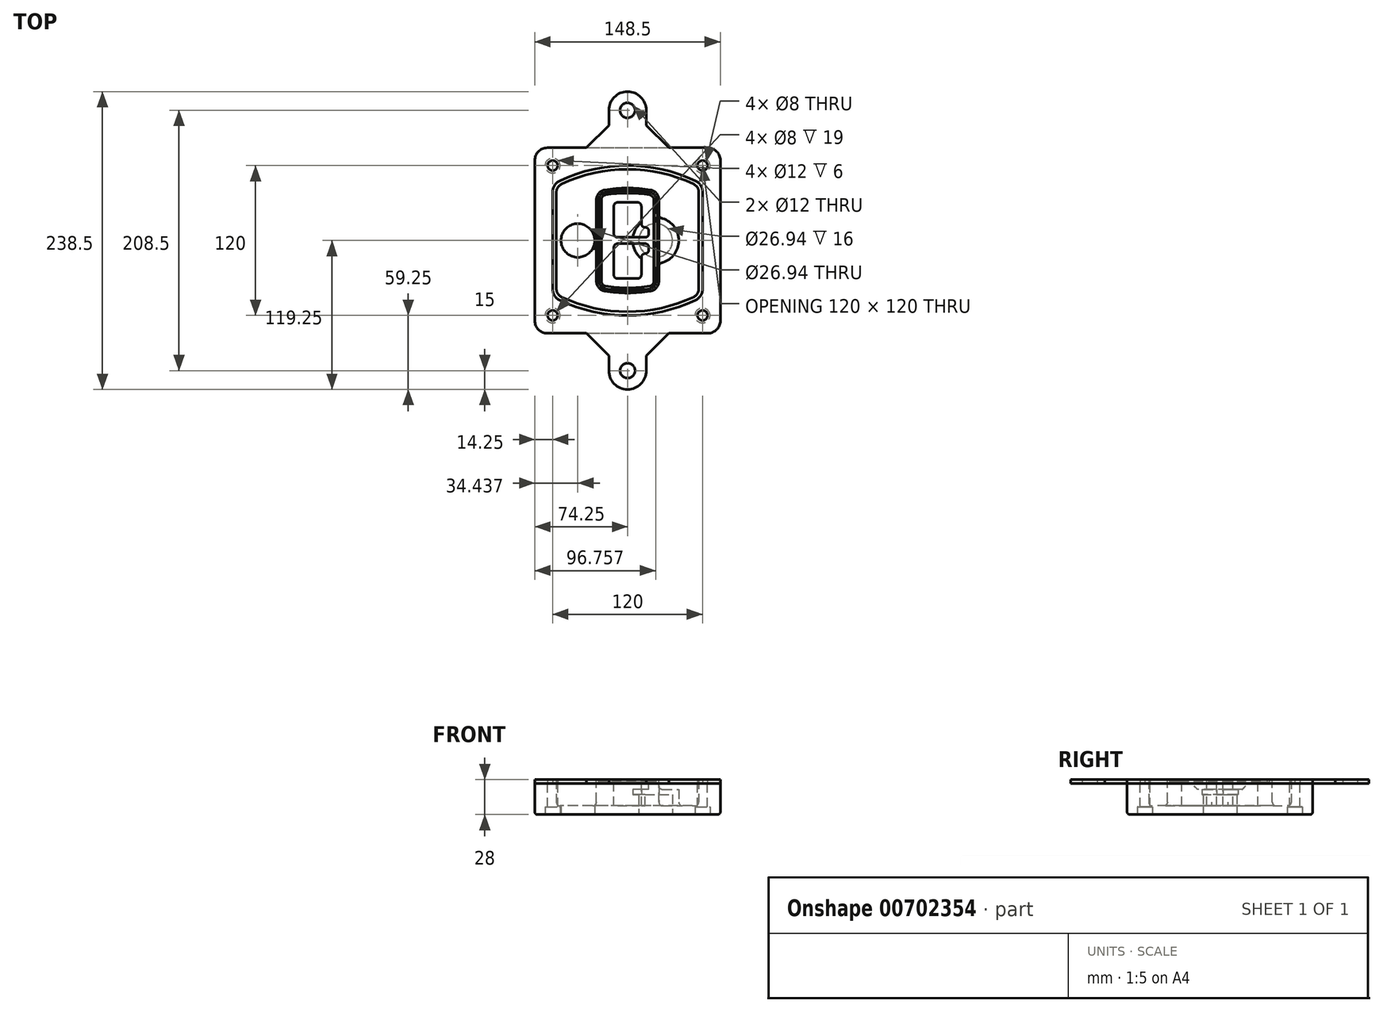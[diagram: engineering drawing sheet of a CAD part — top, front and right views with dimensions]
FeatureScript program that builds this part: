
annotation { "Feature Type Name" : "Feature", "Feature Type Description" : "" }
export const myFeature = defineFeature(function(context is Context, id is Id, definition is map)
    precondition{}
    {
        {
            var Q0;
            Q0=qCreatedBy(makeId("Top.planeOp"),FACE);
            var sketch = newSketch(context, id + "F0", { "sketchPlane" : qUnion([Q0])});
            skPoint(sketch, "E0.rect.middle", {"position": v(0, 0) * mm});
            skLineSegment(sketch, "E1.bottom", {"start": v(-64.25, -74.25) * mm, "end": v(64.25, -74.25) * mm});
            skLineSegment(sketch, "E1.top", {"start": v(-64.25, 74.25) * mm, "end": v(64.25, 74.25) * mm});
            skLineSegment(sketch, "E1.left", {"start": v(-74.25, -64.25) * mm, "end": v(-74.25, 64.25) * mm});
            skLineSegment(sketch, "E1.right", {"start": v(74.25, -64.25) * mm, "end": v(74.25, 64.25) * mm});
            skLineSegment(sketch, "E2", {"start": v(-74.25, 74.25) * mm, "end": v(74.25, -74.25) * mm, "construction": true});
            skLineSegment(sketch, "E3", {"start": v(74.25, 74.25) * mm, "end": v(-74.25, -74.25) * mm, "construction": true});
            skCircle(sketch, "E4", {"center": v(-60, 60) * mm, "radius": 4 * mm});
            skCircle(sketch, "E5", {"center": v(60, 60) * mm, "radius": 4 * mm});
            skCircle(sketch, "E6", {"center": v(60, -60) * mm, "radius": 4 * mm});
            skCircle(sketch, "E7", {"center": v(-60, -60) * mm, "radius": 4 * mm});
            skLineSegment(sketch, "E8", {"start": v(-60, 60) * mm, "end": v(60, 60) * mm, "construction": true});
            skLineSegment(sketch, "E9", {"start": v(60, 60) * mm, "end": v(60, -60) * mm, "construction": true});
            skLineSegment(sketch, "E10", {"start": v(60, -60) * mm, "end": v(-60, -60) * mm, "construction": true});
            skLineSegment(sketch, "E11", {"start": v(-60, -60) * mm, "end": v(-60, 60) * mm, "construction": true});
            skLineSegment(sketch, "E12", {"start": v(-60, 38.83) * mm, "end": v(-60, -38.83) * mm});
            skLineSegment(sketch, "E13", {"start": v(60, 38.83) * mm, "end": v(60, -38.83) * mm});
            skArc(sketch, "E14", {"start": v(54.26, 47.88) * mm, "mid": v(0, 60) * mm, "end": v(-54.26, 47.88) * mm});
            skArc(sketch, "E15", {"start": v(-54.26, -47.88) * mm, "mid": v(0, -60) * mm, "end": v(54.26, -47.88) * mm});
            skLineSegment(sketch, "E16", {"start": v(-60, 0) * mm, "end": v(60, 0) * mm, "construction": true});
            skPoint(sketch, "E17.visualSharp", {"position": v(-60, -45) * mm});
            skArc(sketch, "E17.filletArc", {"start": v(-60, -38.83) * mm, "mid": v(-58.44, -44.2) * mm, "end": v(-54.26, -47.88) * mm});
            skPoint(sketch, "E18.visualSharp", {"position": v(-60, 45) * mm});
            skArc(sketch, "E18.filletArc", {"start": v(-54.26, 47.88) * mm, "mid": v(-58.44, 44.2) * mm, "end": v(-60, 38.83) * mm});
            skPoint(sketch, "E19.visualSharp", {"position": v(60, 45) * mm});
            skArc(sketch, "E19.filletArc", {"start": v(60, 38.83) * mm, "mid": v(58.44, 44.2) * mm, "end": v(54.26, 47.88) * mm});
            skPoint(sketch, "E20.visualSharp", {"position": v(60, -45) * mm});
            skArc(sketch, "E20.filletArc", {"start": v(54.26, -47.88) * mm, "mid": v(58.44, -44.2) * mm, "end": v(60, -38.83) * mm});
            skPoint(sketch, "E21.visualSharp", {"position": v(-74.25, 74.25) * mm});
            skArc(sketch, "E21.filletArc", {"start": v(-64.25, 74.25) * mm, "mid": v(-71.32, 71.32) * mm, "end": v(-74.25, 64.25) * mm});
            skPoint(sketch, "E22.visualSharp", {"position": v(74.25, 74.25) * mm});
            skArc(sketch, "E22.filletArc", {"start": v(74.25, 64.25) * mm, "mid": v(71.32, 71.32) * mm, "end": v(64.25, 74.25) * mm});
            skPoint(sketch, "E23.visualSharp", {"position": v(74.25, -74.25) * mm});
            skArc(sketch, "E23.filletArc", {"start": v(64.25, -74.25) * mm, "mid": v(71.32, -71.32) * mm, "end": v(74.25, -64.25) * mm});
            skPoint(sketch, "E24.visualSharp", {"position": v(-74.25, -74.25) * mm});
            skArc(sketch, "E24.filletArc", {"start": v(-74.25, -64.25) * mm, "mid": v(-71.32, -71.32) * mm, "end": v(-64.25, -74.25) * mm});
            skArc(sketch, "E25.0", {"start": v(57, 38.83) * mm, "mid": v(55.9, 42.58) * mm, "end": v(52.98, 45.17) * mm});
            skLineSegment(sketch, "E25.1", {"start": v(57, 38.83) * mm, "end": v(57, -38.83) * mm});
            skArc(sketch, "E25.2", {"start": v(52.98, -45.17) * mm, "mid": v(55.9, -42.58) * mm, "end": v(57, -38.83) * mm});
            skArc(sketch, "E25.3", {"start": v(-52.98, -45.17) * mm, "mid": v(0, -57) * mm, "end": v(52.98, -45.17) * mm});
            skArc(sketch, "E25.4", {"start": v(-57, -38.83) * mm, "mid": v(-55.9, -42.58) * mm, "end": v(-52.98, -45.17) * mm});
            skArc(sketch, "E25.5", {"start": v(52.98, 45.17) * mm, "mid": v(0, 57) * mm, "end": v(-52.98, 45.17) * mm});
            skLineSegment(sketch, "E25.6", {"start": v(-57, 38.83) * mm, "end": v(-57, -38.83) * mm});
            skArc(sketch, "E25.7", {"start": v(-52.98, 45.17) * mm, "mid": v(-55.9, 42.58) * mm, "end": v(-57, 38.83) * mm});
            skArc(sketch, "E26.0", {"start": v(-55.96, 51.5) * mm, "mid": v(-61.82, 46.33) * mm, "end": v(-64, 38.83) * mm});
            skArc(sketch, "E26.1", {"start": v(55.96, 51.5) * mm, "mid": v(0, 64) * mm, "end": v(-55.96, 51.5) * mm});
            skArc(sketch, "E26.2", {"start": v(64, 38.83) * mm, "mid": v(61.82, 46.33) * mm, "end": v(55.96, 51.5) * mm});
            skLineSegment(sketch, "E26.3", {"start": v(64, 38.83) * mm, "end": v(64, -38.83) * mm});
            skArc(sketch, "E26.4", {"start": v(55.96, -51.5) * mm, "mid": v(61.82, -46.33) * mm, "end": v(64, -38.83) * mm});
            skLineSegment(sketch, "E26.5", {"start": v(-64, 38.83) * mm, "end": v(-64, -38.83) * mm});
            skArc(sketch, "E26.6", {"start": v(-55.96, -51.5) * mm, "mid": v(0, -64) * mm, "end": v(55.96, -51.5) * mm});
            skArc(sketch, "E26.7", {"start": v(-64, -38.83) * mm, "mid": v(-61.82, -46.33) * mm, "end": v(-55.96, -51.5) * mm});
            skSolve(sketch);
        }
        {
            var Q0;
            Q0=makeQuery(id+"F0.imprint","IMPRINT",FACE,{"disambiguationData":[TD([[makeQuery(id+"F0.imprint","IMPRINT",EDGE,{"derivedFrom":sQuery(id+"F0.wireOp",EDGE,"E1.bottom")}),1.0]])]});
            var Q1;
            Q1=makeQuery(id+"F0.imprint","IMPRINT",FACE,{"disambiguationData":[TD([[makeQuery(id+"F0.imprint","IMPRINT",EDGE,{"derivedFrom":sQuery(id+"F0.wireOp",EDGE,"E12")}),1.0]])]});
            var Q2;
            Q2=makeQuery(id+"F0.imprint","IMPRINT",FACE,{"disambiguationData":[TD([[makeQuery(id+"F0.imprint","IMPRINT",EDGE,{"derivedFrom":sQuery(id+"F0.wireOp",EDGE,"E25.0")}),1.0]])]});
            var Q3;
            Q3=makeQuery(id+"F0.imprint","IMPRINT",FACE,{"disambiguationData":[TD([[makeQuery(id+"F0.imprint","IMPRINT",EDGE,{"derivedFrom":sQuery(id+"F0.wireOp",EDGE,"E12")}),-1.0]])]});
            extrude(context, id + "F1", {"entities" : qUnion([Q0, Q1, Q2, Q3]), "oppositeDirection" : true, "depth" : 25 * mm});
        }
        {
            var Q0;
            Q0=makeQuery(id+"F0.imprint","IMPRINT",FACE,{"disambiguationData":[TD([[makeQuery(id+"F0.imprint","IMPRINT",EDGE,{"derivedFrom":sQuery(id+"F0.wireOp",EDGE,"E12")}),1.0]])]});
            extrude(context, id + "F2", {"entities" : qUnion([Q0]), "operationType" : NewBodyOperationType.ADD, "depth" : 3 * mm});
        }
        {
            var Q0;
            Q0=makeQuery(id+"F0.imprint","IMPRINT",FACE,{"disambiguationData":[TD([[makeQuery(id+"F0.imprint","IMPRINT",EDGE,{"derivedFrom":sQuery(id+"F0.wireOp",EDGE,"E25.0")}),1.0]])]});
            extrude(context, id + "F3", {"entities" : qUnion([Q0]), "operationType" : NewBodyOperationType.REMOVE, "oppositeDirection" : true, "depth" : 18 * mm});
        }
        {
            var Q0;
            Q0=makeQuery(id+"F2.opExtrude","CAP_FACE",FACE,{"disambiguationData":[OSD([sQuery(id+"F0.wireOp",EDGE,"E12"),sQuery(id+"F0.wireOp",EDGE,"E13"),sQuery(id+"F0.wireOp",EDGE,"E14"),sQuery(id+"F0.wireOp",EDGE,"E15"),sQuery(id+"F0.wireOp",EDGE,"E17.filletArc"),sQuery(id+"F0.wireOp",EDGE,"E18.filletArc"),sQuery(id+"F0.wireOp",EDGE,"E19.filletArc"),sQuery(id+"F0.wireOp",EDGE,"E20.filletArc"),sQuery(id+"F0.wireOp",EDGE,"E25.0"),sQuery(id+"F0.wireOp",EDGE,"E25.1"),sQuery(id+"F0.wireOp",EDGE,"E25.2"),sQuery(id+"F0.wireOp",EDGE,"E25.3"),sQuery(id+"F0.wireOp",EDGE,"E25.4"),sQuery(id+"F0.wireOp",EDGE,"E25.5"),sQuery(id+"F0.wireOp",EDGE,"E25.6"),sQuery(id+"F0.wireOp",EDGE,"E25.7")])],"isStart":false});
            var sketch = newSketch(context, id + "F4", { "sketchPlane" : qUnion([Q0])});
            skArc(sketch, "E27.0", {"start": v(-18.34, -40.45) * mm, "mid": v(0, -42) * mm, "end": v(18.34, -40.45) * mm});
            skArc(sketch, "E28.0", {"start": v(18.34, 40.45) * mm, "mid": v(0, 42) * mm, "end": v(-18.34, 40.45) * mm});
            skLineSegment(sketch, "E29", {"start": v(-25, 32.57) * mm, "end": v(-25, -32.57) * mm});
            skLineSegment(sketch, "E30", {"start": v(25, 32.57) * mm, "end": v(25, -32.57) * mm});
            skLineSegment(sketch, "E31", {"start": v(-25, 39.1) * mm, "end": v(25, 39.1) * mm, "construction": true});
            skLineSegment(sketch, "E32", {"start": v(-25, -39.1) * mm, "end": v(25, -39.1) * mm, "construction": true});
            skPoint(sketch, "E33.visualSharp", {"position": v(-25, 39.1) * mm});
            skArc(sketch, "E33.filletArc", {"start": v(-18.34, 40.45) * mm, "mid": v(-23.11, 37.73) * mm, "end": v(-25, 32.57) * mm});
            skPoint(sketch, "E34.visualSharp", {"position": v(25, 39.1) * mm});
            skArc(sketch, "E34.filletArc", {"start": v(25, 32.57) * mm, "mid": v(23.11, 37.73) * mm, "end": v(18.34, 40.45) * mm});
            skPoint(sketch, "E35.visualSharp", {"position": v(25, -39.1) * mm});
            skArc(sketch, "E35.filletArc", {"start": v(18.34, -40.45) * mm, "mid": v(23.11, -37.73) * mm, "end": v(25, -32.57) * mm});
            skPoint(sketch, "E36.visualSharp", {"position": v(-25, -39.1) * mm});
            skArc(sketch, "E36.filletArc", {"start": v(-25, -32.57) * mm, "mid": v(-23.11, -37.73) * mm, "end": v(-18.34, -40.45) * mm});
            skArc(sketch, "E37.0", {"start": v(52.98, 45.17) * mm, "mid": v(0, 57) * mm, "end": v(-52.98, 45.17) * mm});
            skArc(sketch, "E37.1", {"start": v(-52.98, 45.17) * mm, "mid": v(-55.9, 42.58) * mm, "end": v(-57, 38.83) * mm});
            skLineSegment(sketch, "E37.2", {"start": v(-57, 38.83) * mm, "end": v(-57, -38.83) * mm});
            skArc(sketch, "E37.3", {"start": v(-57, -38.83) * mm, "mid": v(-55.9, -42.58) * mm, "end": v(-52.98, -45.17) * mm});
            skArc(sketch, "E37.4", {"start": v(-52.98, -45.17) * mm, "mid": v(0, -57) * mm, "end": v(52.98, -45.17) * mm});
            skArc(sketch, "E37.5", {"start": v(52.98, -45.17) * mm, "mid": v(55.9, -42.58) * mm, "end": v(57, -38.83) * mm});
            skLineSegment(sketch, "E37.6", {"start": v(57, 38.83) * mm, "end": v(57, -38.83) * mm});
            skArc(sketch, "E37.7", {"start": v(57, 38.83) * mm, "mid": v(55.9, 42.58) * mm, "end": v(52.98, 45.17) * mm});
            skLineSegment(sketch, "E38.0", {"start": v(23, 32.57) * mm, "end": v(23, -32.57) * mm});
            skArc(sketch, "E38.1", {"start": v(18, -38.48) * mm, "mid": v(21.58, -36.44) * mm, "end": v(23, -32.57) * mm});
            skArc(sketch, "E38.2", {"start": v(-18, -38.48) * mm, "mid": v(0, -40) * mm, "end": v(18, -38.48) * mm});
            skArc(sketch, "E38.3", {"start": v(-23, -32.57) * mm, "mid": v(-21.58, -36.44) * mm, "end": v(-18, -38.48) * mm});
            skLineSegment(sketch, "E38.4", {"start": v(-23, 32.57) * mm, "end": v(-23, -32.57) * mm});
            skArc(sketch, "E38.5", {"start": v(23, 32.57) * mm, "mid": v(21.58, 36.44) * mm, "end": v(18, 38.48) * mm});
            skArc(sketch, "E38.6", {"start": v(-18, 38.48) * mm, "mid": v(-21.58, 36.44) * mm, "end": v(-23, 32.57) * mm});
            skArc(sketch, "E38.7", {"start": v(18, 38.48) * mm, "mid": v(0, 40) * mm, "end": v(-18, 38.48) * mm});
            skArc(sketch, "E39.0", {"start": v(21, 32.57) * mm, "mid": v(20.06, 35.15) * mm, "end": v(17.67, 36.5) * mm});
            skLineSegment(sketch, "E39.1", {"start": v(21, 32.57) * mm, "end": v(21, -32.57) * mm});
            skArc(sketch, "E39.2", {"start": v(17.67, -36.5) * mm, "mid": v(20.06, -35.15) * mm, "end": v(21, -32.57) * mm});
            skArc(sketch, "E39.3", {"start": v(-17.67, -36.5) * mm, "mid": v(0, -38) * mm, "end": v(17.67, -36.5) * mm});
            skArc(sketch, "E39.4", {"start": v(-21, -32.57) * mm, "mid": v(-20.06, -35.15) * mm, "end": v(-17.67, -36.5) * mm});
            skArc(sketch, "E39.5", {"start": v(17.67, 36.5) * mm, "mid": v(0, 38) * mm, "end": v(-17.67, 36.5) * mm});
            skLineSegment(sketch, "E39.6", {"start": v(-21, 32.57) * mm, "end": v(-21, -32.57) * mm});
            skArc(sketch, "E39.7", {"start": v(-17.67, 36.5) * mm, "mid": v(-20.06, 35.15) * mm, "end": v(-21, 32.57) * mm});
            skLineSegment(sketch, "E40", {"start": v(-25, 0) * mm, "end": v(25, 0) * mm, "construction": true});
            skLineSegment(sketch, "E41", {"start": v(-11, 5.5) * mm, "end": v(-11, 27.5) * mm});
            skLineSegment(sketch, "E42", {"start": v(-8, 30.5) * mm, "end": v(8, 30.5) * mm});
            skLineSegment(sketch, "E43", {"start": v(11, 27.5) * mm, "end": v(11, 13.5) * mm});
            skLineSegment(sketch, "E44", {"start": v(14, 10.5) * mm, "end": v(14, 10.5) * mm});
            skLineSegment(sketch, "E45", {"start": v(17, 7.5) * mm, "end": v(17, 5.5) * mm});
            skLineSegment(sketch, "E46", {"start": v(14, 2.5) * mm, "end": v(-8, 2.5) * mm});
            skPoint(sketch, "E47.visualSharp", {"position": v(-11, 30.5) * mm});
            skArc(sketch, "E47.filletArc", {"start": v(-8, 30.5) * mm, "mid": v(-10.12, 29.62) * mm, "end": v(-11, 27.5) * mm});
            skPoint(sketch, "E48.visualSharp", {"position": v(11, 30.5) * mm});
            skArc(sketch, "E48.filletArc", {"start": v(11, 27.5) * mm, "mid": v(10.12, 29.62) * mm, "end": v(8, 30.5) * mm});
            skPoint(sketch, "E49.visualSharp", {"position": v(11, 10.5) * mm});
            skArc(sketch, "E49.filletArc", {"start": v(11, 13.5) * mm, "mid": v(11.88, 11.38) * mm, "end": v(14, 10.5) * mm});
            skPoint(sketch, "E50.visualSharp", {"position": v(17, 10.5) * mm});
            skArc(sketch, "E50.filletArc", {"start": v(17, 7.5) * mm, "mid": v(16.12, 9.62) * mm, "end": v(14, 10.5) * mm});
            skPoint(sketch, "E51.visualSharp", {"position": v(17, 2.5) * mm});
            skArc(sketch, "E51.filletArc", {"start": v(14, 2.5) * mm, "mid": v(16.12, 3.38) * mm, "end": v(17, 5.5) * mm});
            skPoint(sketch, "E52.visualSharp", {"position": v(-11, 2.5) * mm});
            skArc(sketch, "E52.filletArc", {"start": v(-11, 5.5) * mm, "mid": v(-10.12, 3.38) * mm, "end": v(-8, 2.5) * mm});
            skLineSegment(sketch, "E53.0.MirrorCS", {"start": v(14, -2.5) * mm, "end": v(-8, -2.5) * mm});
            skArc(sketch, "E54.0.MirrorCS", {"start": v(-11, -5.5) * mm, "mid": v(-10.12, -3.38) * mm, "end": v(-8, -2.5) * mm});
            skLineSegment(sketch, "E55.0.MirrorCS", {"start": v(-11, -5.5) * mm, "end": v(-11, -27.5) * mm});
            skArc(sketch, "E56.0.MirrorCS", {"start": v(-8, -30.5) * mm, "mid": v(-10.12, -29.62) * mm, "end": v(-11, -27.5) * mm});
            skLineSegment(sketch, "E57.0.MirrorCS", {"start": v(-8, -30.5) * mm, "end": v(8, -30.5) * mm});
            skArc(sketch, "E58.0.MirrorCS", {"start": v(11, -27.5) * mm, "mid": v(10.12, -29.62) * mm, "end": v(8, -30.5) * mm});
            skLineSegment(sketch, "E59.0.MirrorCS", {"start": v(11, -27.5) * mm, "end": v(11, -13.5) * mm});
            skArc(sketch, "E60.0.MirrorCS", {"start": v(11, -13.5) * mm, "mid": v(11.88, -11.38) * mm, "end": v(14, -10.5) * mm});
            skArc(sketch, "E61.0.MirrorCS", {"start": v(17, -7.5) * mm, "mid": v(16.12, -9.62) * mm, "end": v(14, -10.5) * mm});
            skLineSegment(sketch, "E62.0.MirrorCS", {"start": v(17, -7.5) * mm, "end": v(17, -5.5) * mm});
            skArc(sketch, "E63.0.MirrorCS", {"start": v(14, -2.5) * mm, "mid": v(16.12, -3.38) * mm, "end": v(17, -5.5) * mm});
            skSolve(sketch);
        }
        {
            var Q0;
            Q0=makeQuery(id+"F4.imprint","IMPRINT",FACE,{"disambiguationData":[TD([[makeQuery(id+"F4.imprint","IMPRINT",EDGE,{"derivedFrom":sQuery(id+"F4.wireOp",EDGE,"E27.0")}),1.0]])]});
            var Q1;
            Q1=makeQuery(id+"F4.imprint","IMPRINT",FACE,{"disambiguationData":[TD([[makeQuery(id+"F4.imprint","IMPRINT",EDGE,{"derivedFrom":sQuery(id+"F4.wireOp",EDGE,"E38.0")}),-1.0]])]});
            var Q2;
            Q2=makeQuery(id+"F4.imprint","IMPRINT",FACE,{"disambiguationData":[TD([[makeQuery(id+"F4.imprint","IMPRINT",EDGE,{"derivedFrom":sQuery(id+"F4.wireOp",EDGE,"E39.0")}),1.0]])]});
            extrude(context, id + "F5", {"entities" : qUnion([Q0, Q1, Q2]), "operationType" : NewBodyOperationType.ADD, "endBound" : BoundingType.UP_TO_NEXT, "oppositeDirection" : true, "depth" : 25 * mm});
        }
        {
            var Q0;
            Q0=makeQuery(id+"F4.imprint","IMPRINT",FACE,{"disambiguationData":[TD([[makeQuery(id+"F4.imprint","IMPRINT",EDGE,{"derivedFrom":sQuery(id+"F4.wireOp",EDGE,"E38.0")}),-1.0]])]});
            extrude(context, id + "F6", {"entities" : qUnion([Q0]), "operationType" : NewBodyOperationType.REMOVE, "oppositeDirection" : true, "depth" : 2 * mm});
        }
        {
            var Q0;
            Q0=makeQuery(id+"F1.opExtrude","CAP_FACE",FACE,{"disambiguationData":[OSD([sQuery(id+"F0.wireOp",EDGE,"E1.bottom"),sQuery(id+"F0.wireOp",EDGE,"E1.top"),sQuery(id+"F0.wireOp",EDGE,"E1.left"),sQuery(id+"F0.wireOp",EDGE,"E1.right"),sQuery(id+"F0.wireOp",EDGE,"E4"),sQuery(id+"F0.wireOp",EDGE,"E5"),sQuery(id+"F0.wireOp",EDGE,"E6"),sQuery(id+"F0.wireOp",EDGE,"E7"),sQuery(id+"F0.wireOp",EDGE,"E21.filletArc"),sQuery(id+"F0.wireOp",EDGE,"E22.filletArc"),sQuery(id+"F0.wireOp",EDGE,"E23.filletArc"),sQuery(id+"F0.wireOp",EDGE,"E24.filletArc")])],"isStart":false});
            var sketch = newSketch(context, id + "F7", { "sketchPlane" : qUnion([Q0])});
            skCircle(sketch, "E64", {"center": v(22.5, 0) * mm, "radius": 13.47 * mm});
            skCircle(sketch, "E65", {"center": v(-39.81, 0) * mm, "radius": 13.47 * mm});
            skLineSegment(sketch, "E66", {"start": v(74.25, 0) * mm, "end": v(-74.25, 0) * mm});
            skCircle(sketch, "E67", {"center": v(22.5, 0) * mm, "radius": 18.47 * mm});
            skCircle(sketch, "E68", {"center": v(60, -60) * mm, "radius": 6 * mm});
            skCircle(sketch, "E69", {"center": v(-60, -60) * mm, "radius": 6 * mm});
            skCircle(sketch, "E70", {"center": v(-60, 60) * mm, "radius": 6 * mm});
            skCircle(sketch, "E71", {"center": v(60, 60) * mm, "radius": 6 * mm});
            skSolve(sketch);
        }
        {
            var Q0;
            {var subQ1=sQuery(id+"F7.wireOp",EDGE,"E66");var subQ4=sQuery(id+"F7.wireOp",EDGE,"E64");var subQ6=makeQuery(id+"F7.imprint","INTERSECT",VERTEX,{"disambiguationData":[OD(0.0)],"derivedFrom":[subQ4,subQ1]});Q0=makeQuery(id+"F7.imprint","IMPRINT",FACE,{"disambiguationData":[TD([[makeQuery(id+"F7.imprint","IMPRINT",EDGE,{"disambiguationData":[TD([[subQ6,-1.0]])],"derivedFrom":subQ4}),-1.0]])]});}
            var Q1;
            {var subQ0=sQuery(id+"F7.wireOp",EDGE,"E66");var subQ1=sQuery(id+"F7.wireOp",EDGE,"E64");var subQ3=makeQuery(id+"F7.imprint","INTERSECT",VERTEX,{"disambiguationData":[OD(0.0)],"derivedFrom":[subQ1,subQ0]});Q1=makeQuery(id+"F7.imprint","IMPRINT",FACE,{"disambiguationData":[TD([[makeQuery(id+"F7.imprint","IMPRINT",EDGE,{"disambiguationData":[TD([[subQ3,-1.0]])],"derivedFrom":subQ1}),1.0]])]});}
            var Q2;
            {var subQ0=sQuery(id+"F7.wireOp",EDGE,"E66");var subQ1=sQuery(id+"F7.wireOp",EDGE,"E64");var subQ3=makeQuery(id+"F7.imprint","INTERSECT",VERTEX,{"disambiguationData":[OD(0.0)],"derivedFrom":[subQ1,subQ0]});Q2=makeQuery(id+"F7.imprint","IMPRINT",FACE,{"disambiguationData":[TD([[makeQuery(id+"F7.imprint","IMPRINT",EDGE,{"disambiguationData":[TD([[subQ3,1.0]])],"derivedFrom":subQ1}),1.0]])]});}
            var Q3;
            {var subQ1=sQuery(id+"F7.wireOp",EDGE,"E66");var subQ4=sQuery(id+"F7.wireOp",EDGE,"E64");var subQ6=makeQuery(id+"F7.imprint","INTERSECT",VERTEX,{"disambiguationData":[OD(0.0)],"derivedFrom":[subQ4,subQ1]});Q3=makeQuery(id+"F7.imprint","IMPRINT",FACE,{"disambiguationData":[TD([[makeQuery(id+"F7.imprint","IMPRINT",EDGE,{"disambiguationData":[TD([[subQ6,1.0]])],"derivedFrom":subQ4}),-1.0]])]});}
            extrude(context, id + "F8", {"entities" : qUnion([Q0, Q1, Q2, Q3]), "operationType" : NewBodyOperationType.ADD, "oppositeDirection" : true, "depth" : 20 * mm});
        }
        {
            var Q0;
            {var subQ0=sQuery(id+"F7.wireOp",EDGE,"E66");var subQ1=sQuery(id+"F7.wireOp",EDGE,"E64");var subQ3=makeQuery(id+"F7.imprint","INTERSECT",VERTEX,{"disambiguationData":[OD(0.0)],"derivedFrom":[subQ1,subQ0]});Q0=makeQuery(id+"F7.imprint","IMPRINT",FACE,{"disambiguationData":[TD([[makeQuery(id+"F7.imprint","IMPRINT",EDGE,{"disambiguationData":[TD([[subQ3,-1.0]])],"derivedFrom":subQ1}),1.0]])]});}
            var Q1;
            {var subQ0=sQuery(id+"F7.wireOp",EDGE,"E66");var subQ1=sQuery(id+"F7.wireOp",EDGE,"E64");var subQ3=makeQuery(id+"F7.imprint","INTERSECT",VERTEX,{"disambiguationData":[OD(0.0)],"derivedFrom":[subQ1,subQ0]});Q1=makeQuery(id+"F7.imprint","IMPRINT",FACE,{"disambiguationData":[TD([[makeQuery(id+"F7.imprint","IMPRINT",EDGE,{"disambiguationData":[TD([[subQ3,1.0]])],"derivedFrom":subQ1}),1.0]])]});}
            extrude(context, id + "F9", {"entities" : qUnion([Q0, Q1]), "operationType" : NewBodyOperationType.REMOVE, "oppositeDirection" : true, "depth" : 16 * mm});
        }
        {
            var Q0;
            {var subQ0=sQuery(id+"F7.wireOp",EDGE,"E66");var subQ1=sQuery(id+"F7.wireOp",EDGE,"E65");var subQ3=makeQuery(id+"F7.imprint","INTERSECT",VERTEX,{"disambiguationData":[OD(0.0)],"derivedFrom":[subQ1,subQ0]});Q0=makeQuery(id+"F7.imprint","IMPRINT",FACE,{"disambiguationData":[TD([[makeQuery(id+"F7.imprint","IMPRINT",EDGE,{"disambiguationData":[TD([[subQ3,-1.0]])],"derivedFrom":subQ1}),1.0]])]});}
            var Q1;
            {var subQ0=sQuery(id+"F7.wireOp",EDGE,"E66");var subQ1=sQuery(id+"F7.wireOp",EDGE,"E65");var subQ3=makeQuery(id+"F7.imprint","INTERSECT",VERTEX,{"disambiguationData":[OD(0.0)],"derivedFrom":[subQ1,subQ0]});Q1=makeQuery(id+"F7.imprint","IMPRINT",FACE,{"disambiguationData":[TD([[makeQuery(id+"F7.imprint","IMPRINT",EDGE,{"disambiguationData":[TD([[subQ3,1.0]])],"derivedFrom":subQ1}),1.0]])]});}
            extrude(context, id + "F10", {"entities" : qUnion([Q0, Q1]), "operationType" : NewBodyOperationType.REMOVE, "oppositeDirection" : true, "depth" : 25 * mm});
        }
        {
            var Q0;
            Q0=makeQuery(id+"F7.imprint","IMPRINT",FACE,{"disambiguationData":[TD([[makeQuery(id+"F7.imprint","IMPRINT",EDGE,{"derivedFrom":sQuery(id+"F7.wireOp",EDGE,"E68")}),1.0]])]});
            var Q1;
            Q1=makeQuery(id+"F7.imprint","IMPRINT",FACE,{"disambiguationData":[TD([[makeQuery(id+"F7.imprint","IMPRINT",EDGE,{"derivedFrom":makeQuery(id+"F1.opExtrude","CAP_EDGE",EDGE,{"disambiguationData":[OSD([sQuery(id+"F0.wireOp",EDGE,"E5")])],"isStart":false})}),-1.0]])]});
            var Q2;
            Q2=makeQuery(id+"F7.imprint","IMPRINT",FACE,{"disambiguationData":[TD([[makeQuery(id+"F7.imprint","IMPRINT",EDGE,{"derivedFrom":sQuery(id+"F7.wireOp",EDGE,"E69")}),1.0]])]});
            var Q3;
            Q3=makeQuery(id+"F7.imprint","IMPRINT",FACE,{"disambiguationData":[TD([[makeQuery(id+"F7.imprint","IMPRINT",EDGE,{"derivedFrom":makeQuery(id+"F1.opExtrude","CAP_EDGE",EDGE,{"disambiguationData":[OSD([sQuery(id+"F0.wireOp",EDGE,"E4")])],"isStart":false})}),-1.0]])]});
            var Q4;
            Q4=makeQuery(id+"F7.imprint","IMPRINT",FACE,{"disambiguationData":[TD([[makeQuery(id+"F7.imprint","IMPRINT",EDGE,{"derivedFrom":sQuery(id+"F7.wireOp",EDGE,"E70")}),1.0]])]});
            var Q5;
            Q5=makeQuery(id+"F7.imprint","IMPRINT",FACE,{"disambiguationData":[TD([[makeQuery(id+"F7.imprint","IMPRINT",EDGE,{"derivedFrom":makeQuery(id+"F1.opExtrude","CAP_EDGE",EDGE,{"disambiguationData":[OSD([sQuery(id+"F0.wireOp",EDGE,"E7")])],"isStart":false})}),-1.0]])]});
            var Q6;
            Q6=makeQuery(id+"F7.imprint","IMPRINT",FACE,{"disambiguationData":[TD([[makeQuery(id+"F7.imprint","IMPRINT",EDGE,{"derivedFrom":sQuery(id+"F7.wireOp",EDGE,"E71")}),1.0]])]});
            var Q7;
            Q7=makeQuery(id+"F7.imprint","IMPRINT",FACE,{"disambiguationData":[TD([[makeQuery(id+"F7.imprint","IMPRINT",EDGE,{"derivedFrom":makeQuery(id+"F1.opExtrude","CAP_EDGE",EDGE,{"disambiguationData":[OSD([sQuery(id+"F0.wireOp",EDGE,"E6")])],"isStart":false})}),-1.0]])]});
            extrude(context, id + "F11", {"entities" : qUnion([Q0, Q1, Q2, Q3, Q4, Q5, Q6, Q7]), "operationType" : NewBodyOperationType.REMOVE, "oppositeDirection" : true, "depth" : 6 * mm});
        }
        {
            var Q0;
            Q0=makeQuery(id+"F9.boolean.opBoolean","COPY",FACE,{"derivedFrom":makeQuery(id+"F9.opExtrude","CAP_FACE",FACE,{"disambiguationData":[OSD([sQuery(id+"F7.wireOp",EDGE,"E64")])],"isStart":false})});
            var sketch = newSketch(context, id + "F12", { "sketchPlane" : qUnion([Q0])});
            skArc(sketch, "E72.0", {"start": v(11, 14.45) * mm, "mid": v(6.45, 9.13) * mm, "end": v(4.2, 2.5) * mm});
            skArc(sketch, "E72.1", {"start": v(4.2, -2.5) * mm, "mid": v(6.45, -9.13) * mm, "end": v(11, -14.45) * mm});
            skLineSegment(sketch, "E73", {"start": v(4.2, -2.5) * mm, "end": v(14, -2.5) * mm});
            skLineSegment(sketch, "E74.0", {"start": v(14, 2.5) * mm, "end": v(4.2, 2.5) * mm});
            skArc(sketch, "E74.1", {"start": v(14, 2.5) * mm, "mid": v(16.12, 3.38) * mm, "end": v(17, 5.5) * mm});
            skLineSegment(sketch, "E74.2", {"start": v(17, 7.5) * mm, "end": v(17, 5.5) * mm});
            skArc(sketch, "E74.3", {"start": v(17, 7.5) * mm, "mid": v(16.12, 9.62) * mm, "end": v(14, 10.5) * mm});
            skArc(sketch, "E74.4", {"start": v(11, 13.5) * mm, "mid": v(11.88, 11.38) * mm, "end": v(14, 10.5) * mm});
            skLineSegment(sketch, "E74.5", {"start": v(11, 14.45) * mm, "end": v(11, 13.5) * mm});
            skLineSegment(sketch, "E74.7", {"start": v(14, -2.5) * mm, "end": v(4.2, -2.5) * mm});
            skArc(sketch, "E74.8", {"start": v(14, -2.5) * mm, "mid": v(16.12, -3.38) * mm, "end": v(17, -5.5) * mm});
            skLineSegment(sketch, "E74.9", {"start": v(17, -7.5) * mm, "end": v(17, -5.5) * mm});
            skArc(sketch, "E74.10", {"start": v(17, -7.5) * mm, "mid": v(16.12, -9.62) * mm, "end": v(14, -10.5) * mm});
            skArc(sketch, "E74.11", {"start": v(11, -13.5) * mm, "mid": v(11.88, -11.38) * mm, "end": v(14, -10.5) * mm});
            skLineSegment(sketch, "E74.12", {"start": v(11, -14.45) * mm, "end": v(11, -13.5) * mm});
            skPoint(sketch, "E75.orphan", {"position": v(11, -27.5) * mm});
            skPoint(sketch, "E76.orphan", {"position": v(-8, -2.5) * mm});
            skPoint(sketch, "E77.orphan", {"position": v(-8, 2.5) * mm});
            skPoint(sketch, "E78.orphan", {"position": v(11, 27.5) * mm});
            skSolve(sketch);
        }
        {
            var Q0;
            {var subQ7=sQuery(id+"F12.wireOp",EDGE,"E72.0");var subQ14=sQuery(id+"F12.wireOp",EDGE,"E72.1");var subQ16=sQuery(id+"F12.wireOp",EDGE,"E74.1");var subQ18=sQuery(id+"F12.wireOp",EDGE,"E74.8");Q0=qUnion([makeQuery(id+"F12.imprint","IMPRINT",FACE,{"disambiguationData":[TD([[makeQuery(id+"F12.imprint","IMPRINT",EDGE,{"derivedFrom":subQ7}),1.0]])]}),makeQuery(id+"F12.imprint","IMPRINT",FACE,{"disambiguationData":[TD([[makeQuery(id+"F12.imprint","IMPRINT",EDGE,{"derivedFrom":subQ14}),1.0]])]}),makeQuery(id+"F12.imprint","IMPRINT",FACE,{"disambiguationData":[TD([[makeQuery(id+"F12.imprint","IMPRINT",EDGE,{"derivedFrom":subQ16}),1.0]])]}),makeQuery(id+"F12.imprint","IMPRINT",FACE,{"disambiguationData":[TD([[makeQuery(id+"F12.imprint","IMPRINT",EDGE,{"derivedFrom":subQ18}),-1.0]])]})]);}
            var Q1;
            Q1=makeQuery(id+"F5.boolean.opBoolean","SPLIT",FACE,{"disambiguationData":[TD([makeQuery(id+"F5.opExtrude","SWEPT_FACE",FACE,{"disambiguationData":[OSD([sQuery(id+"F4.wireOp",EDGE,"E41")])]})])],"derivedFrom":makeQuery(id+"F3.boolean.opBoolean","COPY",FACE,{"derivedFrom":makeQuery(id+"F3.opExtrude","CAP_FACE",FACE,{"disambiguationData":[OSD([sQuery(id+"F0.wireOp",EDGE,"E25.0"),sQuery(id+"F0.wireOp",EDGE,"E25.1"),sQuery(id+"F0.wireOp",EDGE,"E25.2"),sQuery(id+"F0.wireOp",EDGE,"E25.3"),sQuery(id+"F0.wireOp",EDGE,"E25.4"),sQuery(id+"F0.wireOp",EDGE,"E25.5"),sQuery(id+"F0.wireOp",EDGE,"E25.6"),sQuery(id+"F0.wireOp",EDGE,"E25.7")])],"isStart":false})})});
            extrude(context, id + "F13", {"entities" : qUnion([Q0]), "operationType" : NewBodyOperationType.REMOVE, "endBound" : BoundingType.UP_TO_SURFACE, "endBoundEntityFace" : qUnion([Q1]), "depth" : 25 * mm});
        }
        {
            var Q0;
            Q0=makeQuery(id+"F3.boolean.opBoolean","COPY",EDGE,{"derivedFrom":makeQuery(id+"F3.opExtrude","CAP_EDGE",EDGE,{"disambiguationData":[OSD([sQuery(id+"F0.wireOp",EDGE,"E25.6")])],"isStart":false})});
            var Q1;
            Q1=makeQuery(id+"F8.boolean.opBoolean","INTERSECT",EDGE,{"derivedFrom":[makeQuery(id+"F5.opExtrude","SWEPT_FACE",FACE,{"disambiguationData":[OSD([sQuery(id+"F4.wireOp",EDGE,"E30")])]}),makeQuery(id+"F8.opExtrude","CAP_FACE",FACE,{"disambiguationData":[OSD([sQuery(id+"F7.wireOp",EDGE,"E67")])],"isStart":false})]});
            var Q2;
            Q2=makeQuery(id+"F8.boolean.opBoolean","INTERSECT",EDGE,{"disambiguationData":[OD(1.0)],"derivedFrom":[makeQuery(id+"F5.opExtrude","SWEPT_FACE",FACE,{"disambiguationData":[OSD([sQuery(id+"F4.wireOp",EDGE,"E30")])]}),makeQuery(id+"F8.opExtrude","SWEPT_FACE",FACE,{"disambiguationData":[OSD([sQuery(id+"F7.wireOp",EDGE,"E67")])]})]});
            var Q3;
            {var subQ0=sQuery(id+"F4.wireOp",EDGE,"E30");Q3=makeQuery(id+"F8.boolean.opBoolean","SPLIT",EDGE,{"disambiguationData":[TD([makeQuery(id+"F5.opExtrude","SWEPT_FACE",FACE,{"disambiguationData":[OSD([sQuery(id+"F4.wireOp",EDGE,"E35.filletArc")])]})])],"derivedFrom":makeQuery(id+"F5.opExtrude","CAP_EDGE",EDGE,{"disambiguationData":[OSD([subQ0])],"isStart":false})});}
            var Q4;
            {var subQ0=sQuery(id+"F0.wireOp",EDGE,"E25.7");var subQ1=sQuery(id+"F0.wireOp",EDGE,"E25.1");var subQ2=sQuery(id+"F0.wireOp",EDGE,"E25.6");var subQ3=sQuery(id+"F0.wireOp",EDGE,"E25.5");var subQ4=sQuery(id+"F0.wireOp",EDGE,"E25.4");var subQ5=sQuery(id+"F0.wireOp",EDGE,"E25.0");var subQ6=sQuery(id+"F0.wireOp",EDGE,"E25.2");var subQ7=sQuery(id+"F0.wireOp",EDGE,"E25.3");Q4=makeQuery(id+"F8.boolean.opBoolean","INTERSECT",EDGE,{"derivedFrom":[makeQuery(id+"F5.boolean.opBoolean","SPLIT",FACE,{"disambiguationData":[TD([makeQuery(id+"F2.opExtrude","SWEPT_FACE",FACE,{"disambiguationData":[OSD([subQ5])]})])],"derivedFrom":makeQuery(id+"F3.boolean.opBoolean","COPY",FACE,{"derivedFrom":makeQuery(id+"F3.opExtrude","CAP_FACE",FACE,{"disambiguationData":[OSD([subQ5,subQ1,subQ6,subQ7,subQ4,subQ3,subQ2,subQ0])],"isStart":false})})}),makeQuery(id+"F8.opExtrude","SWEPT_FACE",FACE,{"disambiguationData":[OSD([sQuery(id+"F7.wireOp",EDGE,"E67")])]})]});}
            var Q5;
            Q5=makeQuery(id+"F8.boolean.opBoolean","INTERSECT",EDGE,{"disambiguationData":[OD(0.0)],"derivedFrom":[makeQuery(id+"F5.opExtrude","SWEPT_FACE",FACE,{"disambiguationData":[OSD([sQuery(id+"F4.wireOp",EDGE,"E30")])]}),makeQuery(id+"F8.opExtrude","SWEPT_FACE",FACE,{"disambiguationData":[OSD([sQuery(id+"F7.wireOp",EDGE,"E67")])]})]});
            fillet(context, id + "F14", {"entities" : qUnion([Q0, Q1, Q2, Q3, Q4, Q5]), "radius" : 3 * mm, "tangentPropagation" : true, "allowEdgeOverflow" : false});
        }
        {
            var Q0;
            Q0=makeQuery(id+"F1.opExtrude","CAP_EDGE",EDGE,{"disambiguationData":[OSD([sQuery(id+"F0.wireOp",EDGE,"E1.bottom")])],"isStart":false});
            fillet(context, id + "F15", {"entities" : qUnion([Q0]), "radius" : 2 * mm, "tangentPropagation" : true, "allowEdgeOverflow" : false});
        }
        {
            var Q0;
            {var subQ0=sQuery(id+"F0.wireOp",EDGE,"E21.filletArc");var subQ1=sQuery(id+"F0.wireOp",EDGE,"E7");var subQ2=sQuery(id+"F0.wireOp",EDGE,"E6");var subQ3=sQuery(id+"F0.wireOp",EDGE,"E5");var subQ4=sQuery(id+"F0.wireOp",EDGE,"E4");var subQ5=sQuery(id+"F0.wireOp",EDGE,"E22.filletArc");var subQ6=sQuery(id+"F0.wireOp",EDGE,"E1.bottom");var subQ7=sQuery(id+"F0.wireOp",EDGE,"E1.right");var subQ8=sQuery(id+"F0.wireOp",EDGE,"E1.top");var subQ9=sQuery(id+"F0.wireOp",EDGE,"E1.left");var subQ10=sQuery(id+"F0.wireOp",EDGE,"E23.filletArc");var subQ11=sQuery(id+"F0.wireOp",EDGE,"E24.filletArc");Q0=makeQuery(id+"F2.boolean.opBoolean","SPLIT",FACE,{"disambiguationData":[TD([makeQuery(id+"F1.opExtrude","SWEPT_FACE",FACE,{"disambiguationData":[OSD([subQ6])]})])],"derivedFrom":makeQuery(id+"F1.opExtrude","CAP_FACE",FACE,{"disambiguationData":[OSD([subQ6,subQ8,subQ9,subQ7,subQ4,subQ3,subQ2,subQ1,subQ0,subQ5,subQ10,subQ11])],"isStart":true})});}
            var sketch = newSketch(context, id + "F16", { "sketchPlane" : qUnion([Q0])});
            skLineSegment(sketch, "E79", {"start": v(-15, 104.25) * mm, "end": v(-15, 92.25) * mm});
            skLineSegment(sketch, "E80", {"start": v(-33, 74.25) * mm, "end": v(-15, 92.25) * mm});
            skLineSegment(sketch, "E81", {"start": v(15, 104.25) * mm, "end": v(15, 92.25) * mm});
            skLineSegment(sketch, "E82", {"start": v(33, 74.25) * mm, "end": v(15, 92.25) * mm});
            skArc(sketch, "E83", {"start": v(15, 104.25) * mm, "mid": v(0, 119.25) * mm, "end": v(-15, 104.25) * mm});
            skCircle(sketch, "E84", {"center": v(0, 104.25) * mm, "radius": 6 * mm});
            skLineSegment(sketch, "E85", {"start": v(-33, 74.25) * mm, "end": v(33, 74.25) * mm});
            skLineSegment(sketch, "E86.MirrorCS", {"start": v(-33, -74.25) * mm, "end": v(33, -74.25) * mm});
            skLineSegment(sketch, "E87.MirrorCS", {"start": v(-15, -104.25) * mm, "end": v(-15, -92.25) * mm});
            skLineSegment(sketch, "E88.MirrorCS", {"start": v(-33, -74.25) * mm, "end": v(-15, -92.25) * mm});
            skLineSegment(sketch, "E89.MirrorCS", {"start": v(15, -104.25) * mm, "end": v(15, -92.25) * mm});
            skLineSegment(sketch, "E90.MirrorCS", {"start": v(33, -74.25) * mm, "end": v(15, -92.25) * mm});
            skArc(sketch, "E91.MirrorCS", {"start": v(15, -104.25) * mm, "mid": v(0, -119.25) * mm, "end": v(-15, -104.25) * mm});
            skCircle(sketch, "E92.MirrorC", {"center": v(0, -104.25) * mm, "radius": 6 * mm});
            skSolve(sketch);
        }
        {
            var Q0;
            Q0=makeQuery(id+"F16.imprint","IMPRINT",FACE,{"disambiguationData":[TD([[makeQuery(id+"F16.imprint","IMPRINT",EDGE,{"derivedFrom":sQuery(id+"F16.wireOp",EDGE,"E79")}),1.0]])]});
            var Q1;
            Q1=makeQuery(id+"F16.imprint","IMPRINT",FACE,{"disambiguationData":[TD([[makeQuery(id+"F16.imprint","IMPRINT",EDGE,{"derivedFrom":sQuery(id+"F16.wireOp",EDGE,"E86.MirrorCS")}),-1.0]])]});
            var Q2;
            {var subQ4=sQuery(id+"F16.wireOp",EDGE,"E85");Q2=makeQuery(id+"F16.imprint","IMPRINT",FACE,{"disambiguationData":[TD([[makeQuery(id+"F16.imprint","IMPRINT",EDGE,{"derivedFrom":subQ4}),-1.0]])]});}
            var Q3;
            Q3=makeQuery(id+"F2.opExtrude","CAP_FACE",FACE,{"disambiguationData":[OSD([sQuery(id+"F0.wireOp",EDGE,"E12"),sQuery(id+"F0.wireOp",EDGE,"E13"),sQuery(id+"F0.wireOp",EDGE,"E14"),sQuery(id+"F0.wireOp",EDGE,"E15"),sQuery(id+"F0.wireOp",EDGE,"E17.filletArc"),sQuery(id+"F0.wireOp",EDGE,"E18.filletArc"),sQuery(id+"F0.wireOp",EDGE,"E19.filletArc"),sQuery(id+"F0.wireOp",EDGE,"E20.filletArc"),sQuery(id+"F0.wireOp",EDGE,"E25.0"),sQuery(id+"F0.wireOp",EDGE,"E25.1"),sQuery(id+"F0.wireOp",EDGE,"E25.2"),sQuery(id+"F0.wireOp",EDGE,"E25.3"),sQuery(id+"F0.wireOp",EDGE,"E25.4"),sQuery(id+"F0.wireOp",EDGE,"E25.5"),sQuery(id+"F0.wireOp",EDGE,"E25.6"),sQuery(id+"F0.wireOp",EDGE,"E25.7")])],"isStart":false});
            extrude(context, id + "F17", {"entities" : qUnion([Q0, Q1, Q2]), "endBound" : BoundingType.UP_TO_SURFACE, "depth" : 25 * mm, "endBoundEntityFace" : qUnion([Q3]), "offsetDistance" : 25 * mm});
        }
    });
